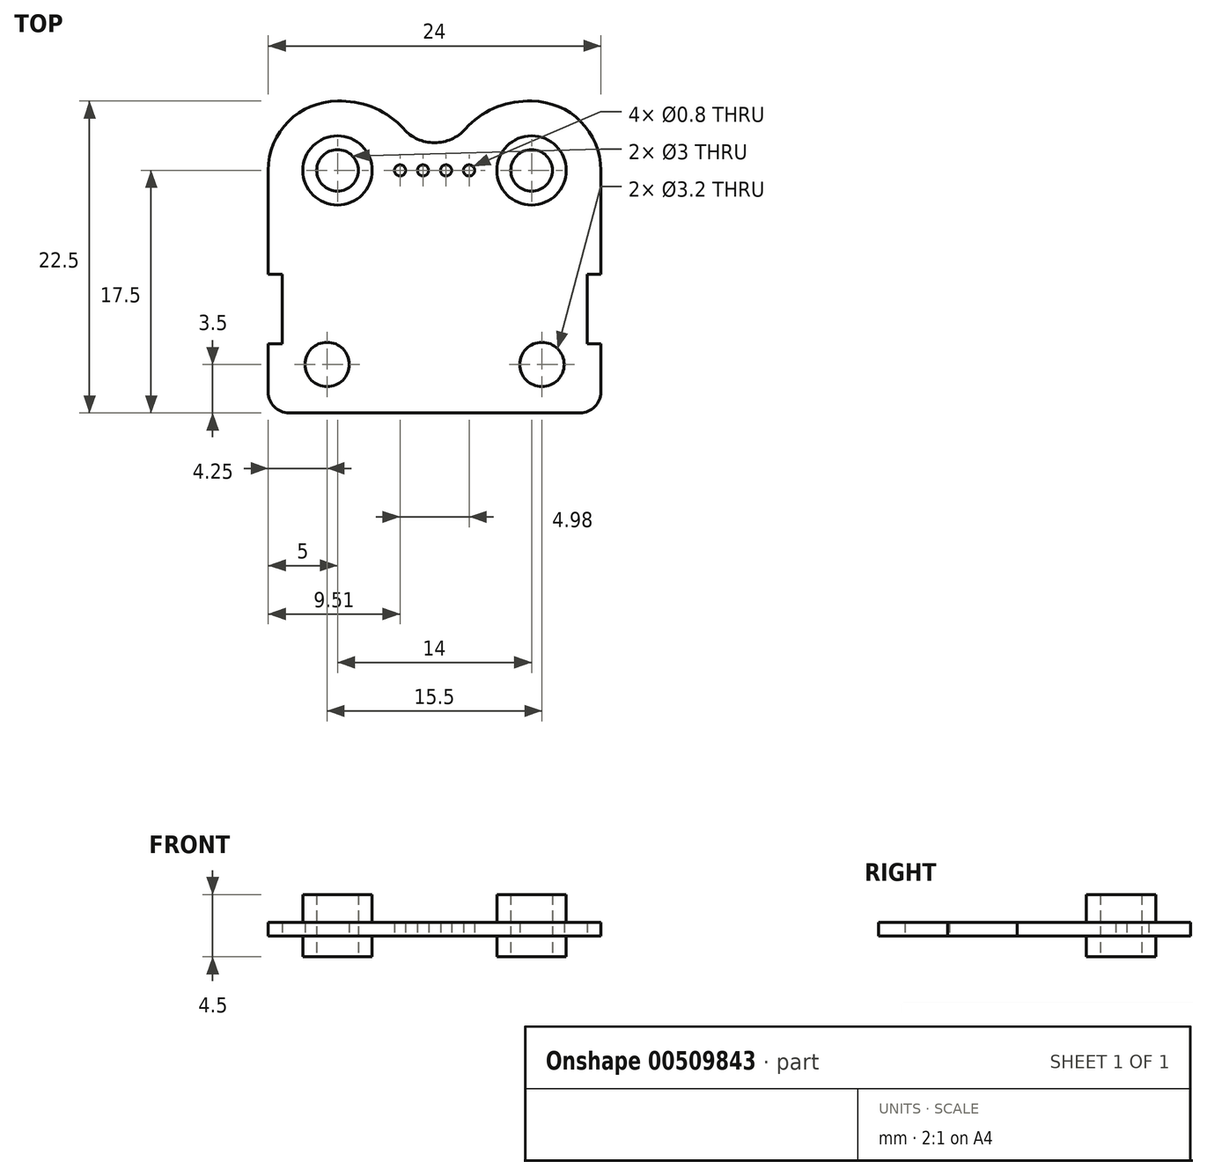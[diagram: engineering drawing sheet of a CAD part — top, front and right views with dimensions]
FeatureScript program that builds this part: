
annotation { "Feature Type Name" : "Feature", "Feature Type Description" : "" }
export const myFeature = defineFeature(function(context is Context, id is Id, definition is map)
    precondition{}
    {
        {
            var Q0;
            Q0=qCreatedBy(makeId("Top.planeOp"),FACE);
            var sketch = newSketch(context, id + "F0", { "sketchPlane" : qUnion([Q0])});
            skLineSegment(sketch, "E0.bottom", {"start": v(12, 2.5) * mm, "end": v(-12, 2.5) * mm});
            skLineSegment(sketch, "E0.top", {"start": v(12, -2.5) * mm, "end": v(-12, -2.5) * mm});
            skLineSegment(sketch, "E0.left", {"start": v(12, 2.5) * mm, "end": v(12, -2.5) * mm});
            skLineSegment(sketch, "E0.right", {"start": v(-12, 2.5) * mm, "end": v(-12, -2.5) * mm});
            skPoint(sketch, "E0.middle", {"position": v(0, 0) * mm});
            skCircle(sketch, "E1", {"center": v(-2.5, 0) * mm, "radius": 0.4 * mm});
            skCircle(sketch, "E2", {"center": v(-0.83, 0) * mm, "radius": 0.4 * mm});
            skCircle(sketch, "E3", {"center": v(0.83, 0) * mm, "radius": 0.4 * mm});
            skCircle(sketch, "E4", {"center": v(2.5, 0) * mm, "radius": 0.4 * mm});
            skCircle(sketch, "E5", {"center": v(-7, 0) * mm, "radius": 1.5 * mm});
            skCircle(sketch, "E6", {"center": v(7, 0) * mm, "radius": 1.5 * mm});
            skSolve(sketch);
        }
        {
            var Q0;
            Q0 = qSketchRegion(id + "F0", true);
            extrude(context, id + "F1", {"entities" : qUnion([Q0]), "depth" : 1 * mm});
        }
        {
            var Q0;
            Q0=makeQuery(id+"F1.opExtrude","SWEPT_FACE",FACE,{"disambiguationData":[OSD([sQuery(id+"F0.wireOp",EDGE,"E0.top")])]});
            var sketch = newSketch(context, id + "F2", { "sketchPlane" : qUnion([Q0])});
            skLineSegment(sketch, "E7.bottom", {"start": v(-12, 1) * mm, "end": v(12, 1) * mm});
            skLineSegment(sketch, "E7.top", {"start": v(-12, 0) * mm, "end": v(12, 0) * mm});
            skLineSegment(sketch, "E7.left", {"start": v(-12, 1) * mm, "end": v(-12, 0) * mm});
            skLineSegment(sketch, "E7.right", {"start": v(12, 1) * mm, "end": v(12, 0) * mm});
            skSolve(sketch);
        }
        {
            var Q0;
            Q0 = qSketchRegion(id + "F2", true);
            extrude(context, id + "F3", {"entities" : qUnion([Q0]), "operationType" : NewBodyOperationType.ADD, "depth" : 15 * mm});
        }
        {
            var Q0;
            Q0=makeQuery(id+"F3.boolean.opBoolean","MERGE",FACE,{"derivedFrom":[makeQuery(id+"F1.opExtrude","CAP_FACE",FACE,{"disambiguationData":[OSD([sQuery(id+"F0.wireOp",EDGE,"E0.bottom"),sQuery(id+"F0.wireOp",EDGE,"E0.top"),sQuery(id+"F0.wireOp",EDGE,"E0.left"),sQuery(id+"F0.wireOp",EDGE,"E0.right"),sQuery(id+"F0.wireOp",EDGE,"E1"),sQuery(id+"F0.wireOp",EDGE,"E2"),sQuery(id+"F0.wireOp",EDGE,"E3"),sQuery(id+"F0.wireOp",EDGE,"E4"),sQuery(id+"F0.wireOp",EDGE,"E5"),sQuery(id+"F0.wireOp",EDGE,"E6")])],"isStart":true}),makeQuery(id+"F3.opExtrude","SWEPT_FACE",FACE,{"disambiguationData":[OSD([sQuery(id+"F2.wireOp",EDGE,"E7.top")])]})]});
            var sketch = newSketch(context, id + "F4", { "sketchPlane" : qUnion([Q0])});
            skCircle(sketch, "E8", {"center": v(-7.75, 14) * mm, "radius": 1.6 * mm});
            skCircle(sketch, "E9", {"center": v(7.75, 14) * mm, "radius": 1.6 * mm});
            skSolve(sketch);
        }
        {
            var Q0;
            Q0 = qSketchRegion(id + "F4", true);
            extrude(context, id + "F5", {"entities" : qUnion([Q0]), "operationType" : NewBodyOperationType.REMOVE, "oppositeDirection" : true, "depth" : 25 * mm});
        }
        {
            var Q0;
            Q0=makeQuery(id+"F3.opExtrude","CAP_EDGE",EDGE,{"disambiguationData":[OSD([sQuery(id+"F2.wireOp",EDGE,"E7.right")])],"isStart":false});
            var Q1;
            Q1=makeQuery(id+"F3.opExtrude","CAP_EDGE",EDGE,{"disambiguationData":[OSD([sQuery(id+"F2.wireOp",EDGE,"E7.left")])],"isStart":false});
            fillet(context, id + "F6", {"entities" : qUnion([Q0, Q1]), "radius" : 1.5 * mm, "tangentPropagation" : true, "allowEdgeOverflow" : false});
        }
        {
            var Q0;
            Q0=makeQuery(id+"F3.boolean.opBoolean","MERGE",FACE,{"derivedFrom":[makeQuery(id+"F1.opExtrude","CAP_FACE",FACE,{"disambiguationData":[OSD([sQuery(id+"F0.wireOp",EDGE,"E0.bottom"),sQuery(id+"F0.wireOp",EDGE,"E0.top"),sQuery(id+"F0.wireOp",EDGE,"E0.left"),sQuery(id+"F0.wireOp",EDGE,"E0.right"),sQuery(id+"F0.wireOp",EDGE,"E1"),sQuery(id+"F0.wireOp",EDGE,"E2"),sQuery(id+"F0.wireOp",EDGE,"E3"),sQuery(id+"F0.wireOp",EDGE,"E4"),sQuery(id+"F0.wireOp",EDGE,"E5"),sQuery(id+"F0.wireOp",EDGE,"E6")])],"isStart":true}),makeQuery(id+"F3.opExtrude","SWEPT_FACE",FACE,{"disambiguationData":[OSD([sQuery(id+"F2.wireOp",EDGE,"E7.top")])]})]});
            var sketch = newSketch(context, id + "F7", { "sketchPlane" : qUnion([Q0])});
            skLineSegment(sketch, "E10.bottom", {"start": v(12, 7.5) * mm, "end": v(11, 7.5) * mm});
            skLineSegment(sketch, "E10.top", {"start": v(12, 12.5) * mm, "end": v(11, 12.5) * mm});
            skLineSegment(sketch, "E10.left", {"start": v(12, 7.5) * mm, "end": v(12, 12.5) * mm});
            skLineSegment(sketch, "E10.right", {"start": v(11, 7.5) * mm, "end": v(11, 12.5) * mm});
            skLineSegment(sketch, "E11.bottom", {"start": v(-12, 7.5) * mm, "end": v(-11, 7.5) * mm});
            skLineSegment(sketch, "E11.top", {"start": v(-12, 12.5) * mm, "end": v(-11, 12.5) * mm});
            skLineSegment(sketch, "E11.left", {"start": v(-12, 7.5) * mm, "end": v(-12, 12.5) * mm});
            skLineSegment(sketch, "E11.right", {"start": v(-11, 7.5) * mm, "end": v(-11, 12.5) * mm});
            skSolve(sketch);
        }
        {
            var Q0;
            Q0 = qSketchRegion(id + "F7", true);
            var Q1;
            Q1=makeQuery(id+"F3.boolean.opBoolean","MERGE",FACE,{"derivedFrom":[makeQuery(id+"F1.opExtrude","CAP_FACE",FACE,{"disambiguationData":[OSD([sQuery(id+"F0.wireOp",EDGE,"E0.bottom"),sQuery(id+"F0.wireOp",EDGE,"E0.top"),sQuery(id+"F0.wireOp",EDGE,"E0.left"),sQuery(id+"F0.wireOp",EDGE,"E0.right"),sQuery(id+"F0.wireOp",EDGE,"E1"),sQuery(id+"F0.wireOp",EDGE,"E2"),sQuery(id+"F0.wireOp",EDGE,"E3"),sQuery(id+"F0.wireOp",EDGE,"E4"),sQuery(id+"F0.wireOp",EDGE,"E5"),sQuery(id+"F0.wireOp",EDGE,"E6")])],"isStart":false}),makeQuery(id+"F3.opExtrude","SWEPT_FACE",FACE,{"disambiguationData":[OSD([sQuery(id+"F2.wireOp",EDGE,"E7.bottom")])]})]});
            extrude(context, id + "F8", {"entities" : qUnion([Q0]), "operationType" : NewBodyOperationType.REMOVE, "endBound" : BoundingType.UP_TO_SURFACE, "oppositeDirection" : true, "endBoundEntityFace" : qUnion([Q1]), "depth" : 25 * mm});
        }
        {
            var Q0;
            Q0=makeQuery(id+"F1.opExtrude","SWEPT_FACE",FACE,{"disambiguationData":[OSD([sQuery(id+"F0.wireOp",EDGE,"E0.bottom")])]});
            var sketch = newSketch(context, id + "F9", { "sketchPlane" : qUnion([Q0])});
            skLineSegment(sketch, "E12.bottom", {"start": v(-12, 1) * mm, "end": v(12, 1) * mm});
            skLineSegment(sketch, "E12.top", {"start": v(-12, 0) * mm, "end": v(12, 0) * mm});
            skLineSegment(sketch, "E12.left", {"start": v(-12, 1) * mm, "end": v(-12, 0) * mm});
            skLineSegment(sketch, "E12.right", {"start": v(12, 1) * mm, "end": v(12, 0) * mm});
            skSolve(sketch);
        }
        {
            var Q0;
            Q0 = qSketchRegion(id + "F9", true);
            extrude(context, id + "F10", {"entities" : qUnion([Q0]), "operationType" : NewBodyOperationType.ADD, "depth" : 2.5 * mm});
        }
        {
            var Q0;
            Q0=makeQuery(id+"F10.opExtrude","CAP_EDGE",EDGE,{"disambiguationData":[OSD([sQuery(id+"F9.wireOp",EDGE,"E12.right")])],"isStart":false});
            var Q1;
            Q1=makeQuery(id+"F10.opExtrude","CAP_EDGE",EDGE,{"disambiguationData":[OSD([sQuery(id+"F9.wireOp",EDGE,"E12.left")])],"isStart":false});
            fillet(context, id + "F11", {"entities" : qUnion([Q0, Q1]), "radius" : 5 * mm, "tangentPropagation" : true, "allowEdgeOverflow" : false});
        }
        {
            var Q0;
            Q0=makeQuery(id+"F10.boolean.opBoolean","MERGE",FACE,{"derivedFrom":[makeQuery(id+"F3.boolean.opBoolean","MERGE",FACE,{"derivedFrom":[makeQuery(id+"F1.opExtrude","CAP_FACE",FACE,{"disambiguationData":[OSD([sQuery(id+"F0.wireOp",EDGE,"E0.bottom"),sQuery(id+"F0.wireOp",EDGE,"E0.top"),sQuery(id+"F0.wireOp",EDGE,"E0.left"),sQuery(id+"F0.wireOp",EDGE,"E0.right"),sQuery(id+"F0.wireOp",EDGE,"E1"),sQuery(id+"F0.wireOp",EDGE,"E2"),sQuery(id+"F0.wireOp",EDGE,"E3"),sQuery(id+"F0.wireOp",EDGE,"E4"),sQuery(id+"F0.wireOp",EDGE,"E5"),sQuery(id+"F0.wireOp",EDGE,"E6")])],"isStart":true}),makeQuery(id+"F3.opExtrude","SWEPT_FACE",FACE,{"disambiguationData":[OSD([sQuery(id+"F2.wireOp",EDGE,"E7.top")])]})]}),makeQuery(id+"F10.opExtrude","SWEPT_FACE",FACE,{"disambiguationData":[OSD([sQuery(id+"F9.wireOp",EDGE,"E12.top")])]})]});
            var sketch = newSketch(context, id + "F12", { "sketchPlane" : qUnion([Q0])});
            skCircle(sketch, "E13", {"center": v(7, 0) * mm, "radius": 1.5 * mm});
            skCircle(sketch, "E14", {"center": v(7, 0) * mm, "radius": 2.5 * mm});
            skCircle(sketch, "E15", {"center": v(-7, 0) * mm, "radius": 1.5 * mm});
            skCircle(sketch, "E16", {"center": v(-7, 0) * mm, "radius": 2.5 * mm});
            skSolve(sketch);
        }
        {
            var Q0;
            Q0 = qSketchRegion(id + "F12", true);
            extrude(context, id + "F13", {"entities" : qUnion([Q0]), "operationType" : NewBodyOperationType.ADD, "depth" : 1.5 * mm});
        }
        {
            var Q0;
            Q0=makeQuery(id+"F10.boolean.opBoolean","MERGE",FACE,{"derivedFrom":[makeQuery(id+"F3.boolean.opBoolean","MERGE",FACE,{"derivedFrom":[makeQuery(id+"F1.opExtrude","CAP_FACE",FACE,{"disambiguationData":[OSD([sQuery(id+"F0.wireOp",EDGE,"E0.bottom"),sQuery(id+"F0.wireOp",EDGE,"E0.top"),sQuery(id+"F0.wireOp",EDGE,"E0.left"),sQuery(id+"F0.wireOp",EDGE,"E0.right"),sQuery(id+"F0.wireOp",EDGE,"E1"),sQuery(id+"F0.wireOp",EDGE,"E2"),sQuery(id+"F0.wireOp",EDGE,"E3"),sQuery(id+"F0.wireOp",EDGE,"E4"),sQuery(id+"F0.wireOp",EDGE,"E5"),sQuery(id+"F0.wireOp",EDGE,"E6")])],"isStart":false}),makeQuery(id+"F3.opExtrude","SWEPT_FACE",FACE,{"disambiguationData":[OSD([sQuery(id+"F2.wireOp",EDGE,"E7.bottom")])]})]}),makeQuery(id+"F10.opExtrude","SWEPT_FACE",FACE,{"disambiguationData":[OSD([sQuery(id+"F9.wireOp",EDGE,"E12.bottom")])]})]});
            var sketch = newSketch(context, id + "F14", { "sketchPlane" : qUnion([Q0])});
            skCircle(sketch, "E17", {"center": v(7, 0) * mm, "radius": 1.5 * mm});
            skCircle(sketch, "E18", {"center": v(7, 0) * mm, "radius": 2.5 * mm});
            skCircle(sketch, "E19", {"center": v(-7, 0) * mm, "radius": 1.5 * mm});
            skCircle(sketch, "E20", {"center": v(-7, 0) * mm, "radius": 2.5 * mm});
            skSolve(sketch);
        }
        {
            var Q0;
            Q0 = qSketchRegion(id + "F14", true);
            extrude(context, id + "F15", {"entities" : qUnion([Q0]), "operationType" : NewBodyOperationType.ADD, "depth" : 2 * mm});
        }
        {
            var Q0;
            Q0=makeQuery(id+"F10.boolean.opBoolean","MERGE",FACE,{"derivedFrom":[makeQuery(id+"F3.boolean.opBoolean","MERGE",FACE,{"derivedFrom":[makeQuery(id+"F1.opExtrude","CAP_FACE",FACE,{"disambiguationData":[OSD([sQuery(id+"F0.wireOp",EDGE,"E0.bottom"),sQuery(id+"F0.wireOp",EDGE,"E0.top"),sQuery(id+"F0.wireOp",EDGE,"E0.left"),sQuery(id+"F0.wireOp",EDGE,"E0.right"),sQuery(id+"F0.wireOp",EDGE,"E1"),sQuery(id+"F0.wireOp",EDGE,"E2"),sQuery(id+"F0.wireOp",EDGE,"E3"),sQuery(id+"F0.wireOp",EDGE,"E4"),sQuery(id+"F0.wireOp",EDGE,"E5"),sQuery(id+"F0.wireOp",EDGE,"E6")])],"isStart":true}),makeQuery(id+"F3.opExtrude","SWEPT_FACE",FACE,{"disambiguationData":[OSD([sQuery(id+"F2.wireOp",EDGE,"E7.top")])]})]}),makeQuery(id+"F10.opExtrude","SWEPT_FACE",FACE,{"disambiguationData":[OSD([sQuery(id+"F9.wireOp",EDGE,"E12.top")])]})]});
            var sketch = newSketch(context, id + "F16", { "sketchPlane" : qUnion([Q0])});
            skCircle(sketch, "E21", {"center": v(0, -5) * mm, "radius": 3 * mm});
            skSolve(sketch);
        }
        {
            var Q0;
            Q0 = qSketchRegion(id + "F16", true);
            extrude(context, id + "F17", {"entities" : qUnion([Q0]), "operationType" : NewBodyOperationType.REMOVE, "oppositeDirection" : true, "depth" : 25 * mm});
        }
        {
            var Q0;
            Q0=makeQuery(id+"F17.boolean.opBoolean","INTERSECT",EDGE,{"disambiguationData":[OD(0.0)],"derivedFrom":[makeQuery(id+"F10.opExtrude","CAP_FACE",FACE,{"disambiguationData":[OSD([sQuery(id+"F9.wireOp",EDGE,"E12.bottom"),sQuery(id+"F9.wireOp",EDGE,"E12.top"),sQuery(id+"F9.wireOp",EDGE,"E12.left"),sQuery(id+"F9.wireOp",EDGE,"E12.right")])],"isStart":false}),makeQuery(id+"F17.opExtrude","SWEPT_FACE",FACE,{"disambiguationData":[OSD([sQuery(id+"F16.wireOp",EDGE,"E21")])]})]});
            var Q1;
            Q1=makeQuery(id+"F17.boolean.opBoolean","INTERSECT",EDGE,{"disambiguationData":[OD(1.0)],"derivedFrom":[makeQuery(id+"F10.opExtrude","CAP_FACE",FACE,{"disambiguationData":[OSD([sQuery(id+"F9.wireOp",EDGE,"E12.bottom"),sQuery(id+"F9.wireOp",EDGE,"E12.top"),sQuery(id+"F9.wireOp",EDGE,"E12.left"),sQuery(id+"F9.wireOp",EDGE,"E12.right")])],"isStart":false}),makeQuery(id+"F17.opExtrude","SWEPT_FACE",FACE,{"disambiguationData":[OSD([sQuery(id+"F16.wireOp",EDGE,"E21")])]})]});
            fillet(context, id + "F18", {"entities" : qUnion([Q0, Q1]), "radius" : 6 * mm, "tangentPropagation" : true, "allowEdgeOverflow" : false});
        }
    });
